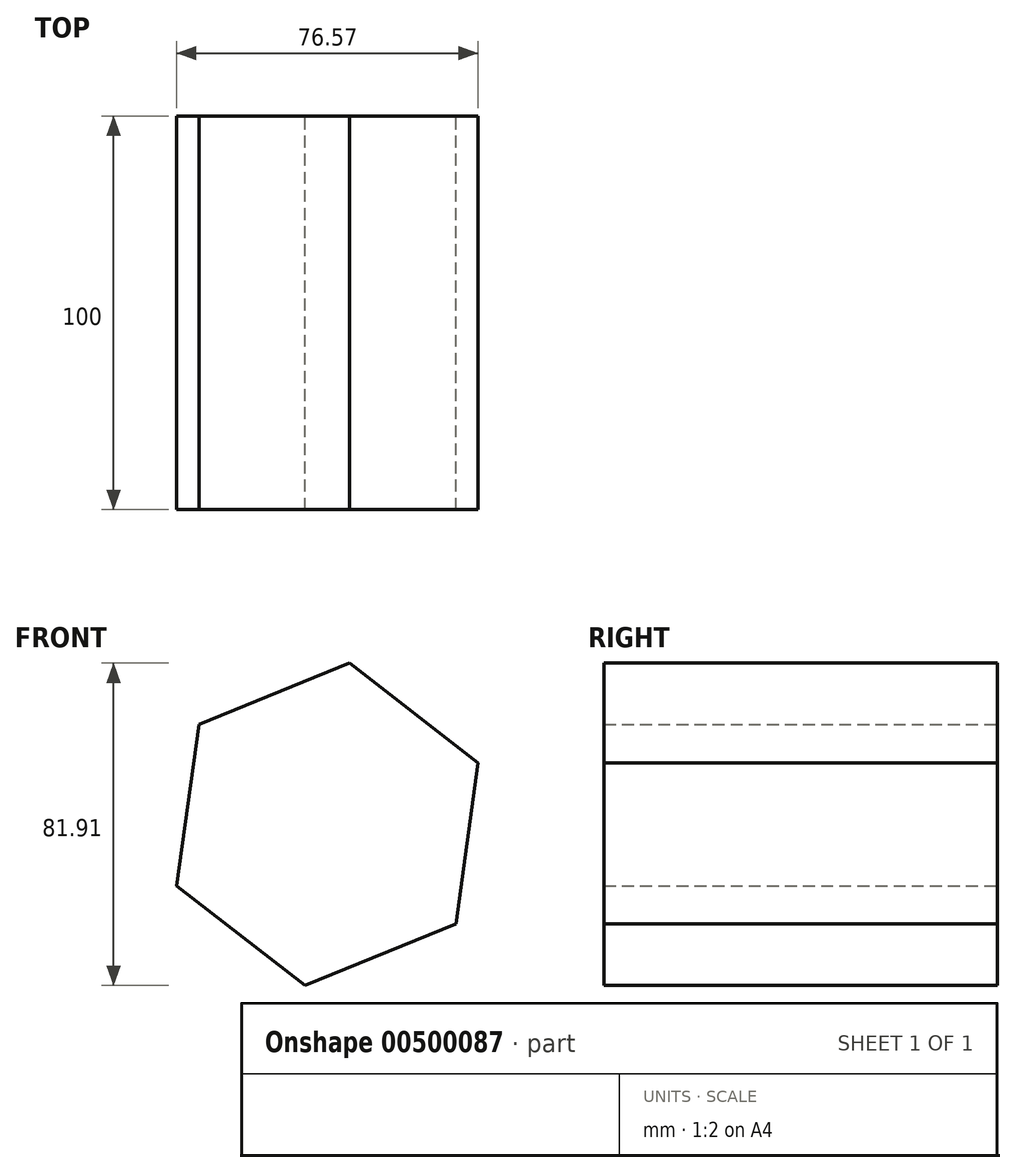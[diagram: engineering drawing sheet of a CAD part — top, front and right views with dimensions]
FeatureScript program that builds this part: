
annotation { "Feature Type Name" : "Feature", "Feature Type Description" : "" }
export const myFeature = defineFeature(function(context is Context, id is Id, definition is map)
    precondition{}
    {
        {
            var Q0;
            Q0=qCreatedBy(makeId("Front.planeOp"),FACE);
            var sketch = newSketch(context, id + "F0", { "sketchPlane" : qUnion([Q0])});
            skCircle(sketch, "E0.cCircle", {"center": v(-36.73, 31.63) * mm, "radius": 41.34 * mm, "construction": true});
            skLineSegment(sketch, "E0.0", {"start": v(-4.08, 6.27) * mm, "end": v(-42.36, -9.33) * mm});
            skLineSegment(sketch, "E0.1", {"start": v(-42.36, -9.33) * mm, "end": v(-75, 16.03) * mm});
            skLineSegment(sketch, "E0.2", {"start": v(-75, 16.03) * mm, "end": v(-69.37, 56.98) * mm});
            skLineSegment(sketch, "E0.3", {"start": v(-69.37, 56.98) * mm, "end": v(-31.09, 72.58) * mm});
            skLineSegment(sketch, "E0.4", {"start": v(-31.09, 72.58) * mm, "end": v(1.56, 47.22) * mm});
            skLineSegment(sketch, "E0.5", {"start": v(1.56, 47.22) * mm, "end": v(-4.08, 6.27) * mm});
            skSolve(sketch);
        }
        {
            var Q0;
            Q0=makeQuery(id+"F0.imprint","IMPRINT",FACE,{"disambiguationData":[TD([[makeQuery(id+"F0.imprint","IMPRINT",EDGE,{"derivedFrom":sQuery(id+"F0.wireOp",EDGE,"E0.0")}),-1.0]])]});
            extrude(context, id + "F1", {"entities" : qUnion([Q0]), "endBound" : BoundingType.SYMMETRIC, "depth" : 100 * mm});
        }
    });
